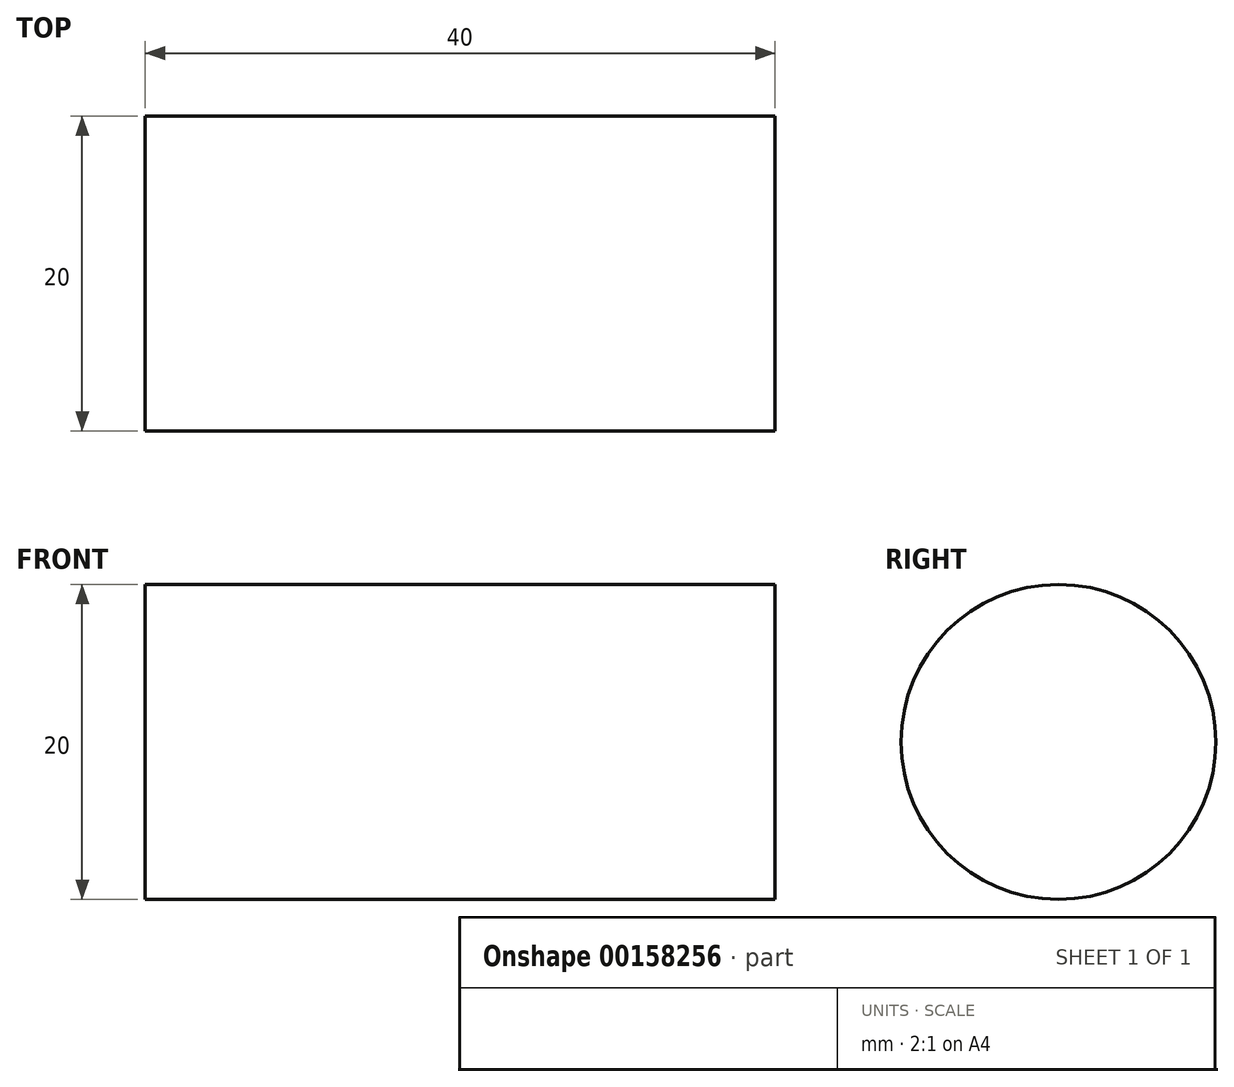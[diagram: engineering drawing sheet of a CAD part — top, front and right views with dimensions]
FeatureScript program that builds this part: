
annotation { "Feature Type Name" : "Feature", "Feature Type Description" : "" }
export const myFeature = defineFeature(function(context is Context, id is Id, definition is map)
    precondition{}
    {
        {
            var Q0;
            Q0=qCreatedBy(makeId("Right.planeOp"),FACE);
            var sketch = newSketch(context, id + "F0", { "sketchPlane" : qUnion([Q0])});
            skCircle(sketch, "E0", {"center": v(0, 0) * mm, "radius": 10 * mm});
            skSolve(sketch);
        }
        {
            var Q0;
            Q0=makeQuery(id+"F0.imprint","IMPRINT",FACE,{"disambiguationData":[TD([[makeQuery(id+"F0.imprint","IMPRINT",EDGE,{"derivedFrom":sQuery(id+"F0.wireOp",EDGE,"E0")}),1.0]])]});
            extrude(context, id + "F1", {"entities" : qUnion([Q0]), "endBound" : BoundingType.SYMMETRIC, "depth" : 40 * mm});
        }
    });
